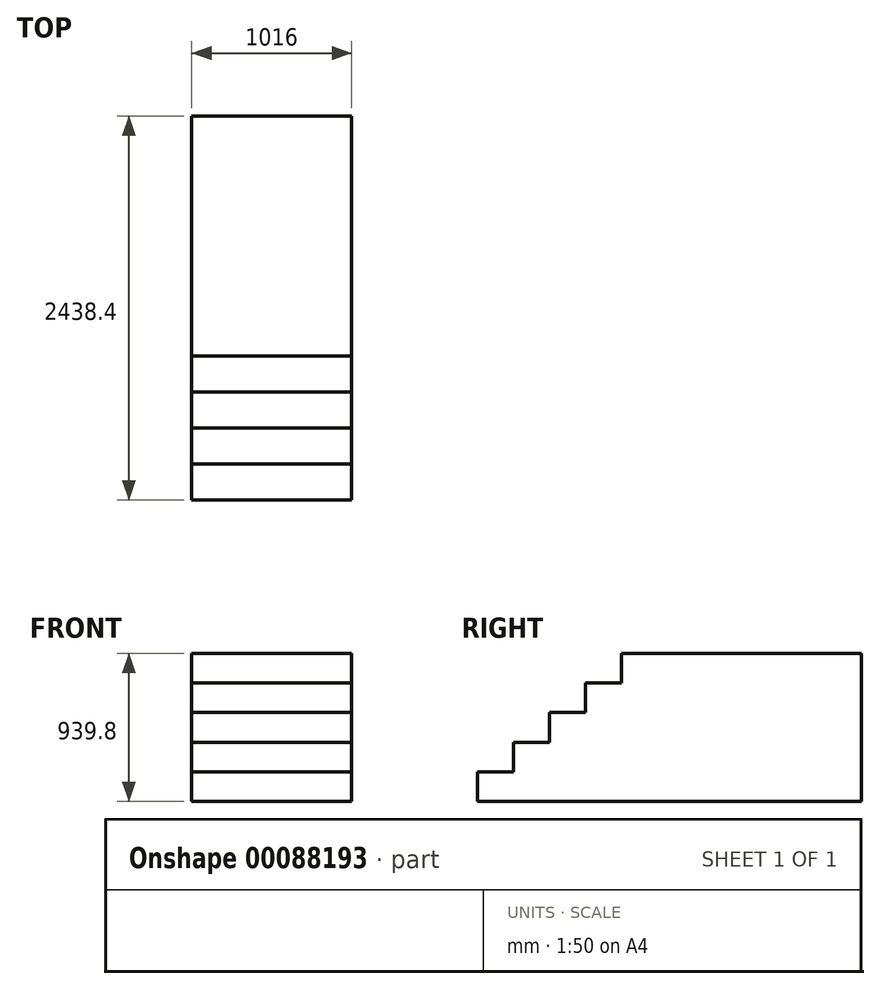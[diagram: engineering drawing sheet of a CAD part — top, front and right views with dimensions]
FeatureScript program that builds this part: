
annotation { "Feature Type Name" : "Feature", "Feature Type Description" : "" }
export const myFeature = defineFeature(function(context is Context, id is Id, definition is map)
    precondition{}
    {
        {
            var Q0;
            Q0=qCreatedBy(makeId("Top.planeOp"),FACE);
            var sketch = newSketch(context, id + "F0", { "sketchPlane" : qUnion([Q0])});
            skLineSegment(sketch, "E0.bottom", {"start": v(2438.4, -533.4) * mm, "end": v(-2438.4, -533.4) * mm});
            skLineSegment(sketch, "E0.top", {"start": v(2438.4, 533.4) * mm, "end": v(-2438.4, 533.4) * mm});
            skLineSegment(sketch, "E0.left", {"start": v(2438.4, -533.4) * mm, "end": v(2438.4, 533.4) * mm});
            skLineSegment(sketch, "E0.right", {"start": v(-2438.4, -533.4) * mm, "end": v(-2438.4, 533.4) * mm});
            skPoint(sketch, "E0.middle", {"position": v(0, 0) * mm});
            skSolve(sketch);
        }
        {
            var Q0;
            Q0=qSketchRegion(id+"F0",true);
            extrude(context, id + "F1", {"entities" : qUnion([Q0]), "oppositeDirection" : true, "depth" : 101.6 * mm});
        }
        {
            var Q0;
            Q0=makeQuery(id+"F1.opExtrude","SWEPT_FACE",FACE,{"disambiguationData":[OSD([sQuery(id+"F0.wireOp",EDGE,"E0.right")])]});
            var sketch = newSketch(context, id + "F2", { "sketchPlane" : qUnion([Q0])});
            skLineSegment(sketch, "E1", {"start": v(533.4, 0) * mm, "end": v(533.4, -187.96) * mm});
            skLineSegment(sketch, "E2", {"start": v(533.4, -187.96) * mm, "end": v(762, -187.96) * mm});
            skLineSegment(sketch, "E3", {"start": v(762, -187.96) * mm, "end": v(762, -375.92) * mm});
            skLineSegment(sketch, "E4", {"start": v(762, -375.92) * mm, "end": v(990.6, -375.92) * mm});
            skLineSegment(sketch, "E5", {"start": v(990.6, -375.92) * mm, "end": v(990.6, -563.88) * mm});
            skLineSegment(sketch, "E6", {"start": v(990.6, -563.88) * mm, "end": v(1219.2, -563.88) * mm});
            skLineSegment(sketch, "E7", {"start": v(1447.8, -751.84) * mm, "end": v(1447.8, -939.8) * mm});
            skLineSegment(sketch, "E8", {"start": v(1447.8, -939.8) * mm, "end": v(304.8, -939.8) * mm});
            skLineSegment(sketch, "E9", {"start": v(304.8, -939.8) * mm, "end": v(304.8, 0) * mm, "construction": true});
            skLineSegment(sketch, "E10", {"start": v(304.8, 0) * mm, "end": v(533.4, 0) * mm});
            skLineSegment(sketch, "E11", {"start": v(1219.2, -563.88) * mm, "end": v(1219.2, -751.84) * mm});
            skLineSegment(sketch, "E12", {"start": v(1219.2, -751.84) * mm, "end": v(1447.8, -751.84) * mm});
            skLineSegment(sketch, "E13", {"start": v(304.8, -939.8) * mm, "end": v(-533.4, -939.8) * mm});
            skLineSegment(sketch, "E14", {"start": v(-533.4, -939.8) * mm, "end": v(-533.4, 0) * mm});
            skLineSegment(sketch, "E15", {"start": v(-533.4, 0) * mm, "end": v(304.8, 0) * mm});
            skSolve(sketch);
        }
        {
            var Q0;
            Q0=qSketchRegion(id+"F2",true);
            extrude(context, id + "F3", {"entities" : qUnion([Q0]), "operationType" : NewBodyOperationType.ADD, "oppositeDirection" : true, "depth" : 1016 * mm});
        }
        {
            var Q0;
            Q0=makeQuery(id+"F3.boolean.opBoolean","MERGE",FACE,{"derivedFrom":[makeQuery(id+"F1.opExtrude","SWEPT_FACE",FACE,{"disambiguationData":[OSD([sQuery(id+"F0.wireOp",EDGE,"E0.bottom")])]}),makeQuery(id+"F3.opExtrude","SWEPT_FACE",FACE,{"disambiguationData":[OSD([sQuery(id+"F2.wireOp",EDGE,"E1")])]})]});
            var sketch = newSketch(context, id + "F4", { "sketchPlane" : qUnion([Q0])});
            skLineSegment(sketch, "E16.0", {"start": v(-1422.4, -101.6) * mm, "end": v(-1422.4, -187.96) * mm});
            skLineSegment(sketch, "E17", {"start": v(-1422.4, -101.6) * mm, "end": v(762, -101.6) * mm});
            skLineSegment(sketch, "E18", {"start": v(762, -101.6) * mm, "end": v(762, -939.8) * mm});
            skLineSegment(sketch, "E19", {"start": v(762, -939.8) * mm, "end": v(-1422.4, -939.8) * mm});
            skLineSegment(sketch, "E20", {"start": v(-1422.4, -187.96) * mm, "end": v(-1422.4, -939.8) * mm});
            skLineSegment(sketch, "E21.bottom", {"start": v(-812.8, -939.8) * mm, "end": v(-355.6, -939.8) * mm});
            skLineSegment(sketch, "E21.top", {"start": v(-812.8, -228.6) * mm, "end": v(-355.6, -228.6) * mm});
            skLineSegment(sketch, "E21.left", {"start": v(-812.8, -939.8) * mm, "end": v(-812.8, -228.6) * mm});
            skLineSegment(sketch, "E21.right", {"start": v(-355.6, -939.8) * mm, "end": v(-355.6, -228.6) * mm});
            skLineSegment(sketch, "E22.bottom", {"start": v(-304.8, -939.8) * mm, "end": v(152.4, -939.8) * mm});
            skLineSegment(sketch, "E22.top", {"start": v(-304.8, -228.6) * mm, "end": v(152.4, -228.6) * mm});
            skLineSegment(sketch, "E22.left", {"start": v(-304.8, -939.8) * mm, "end": v(-304.8, -228.6) * mm});
            skLineSegment(sketch, "E22.right", {"start": v(152.4, -939.8) * mm, "end": v(152.4, -228.6) * mm});
            skSolve(sketch);
        }
        {
            var Q0;
            Q0=makeQuery(id+"F4.imprint","IMPRINT",FACE,{"disambiguationData":[TD([[makeQuery(id+"F4.imprint","IMPRINT",EDGE,{"derivedFrom":sQuery(id+"F4.wireOp",EDGE,"E16.0")}),1.0]])]});
            extrude(context, id + "F5", {"entities" : qUnion([Q0]), "operationType" : NewBodyOperationType.ADD, "oppositeDirection" : true, "depth" : 101.6 * mm});
        }
        {
            var Q0;
            Q0=makeQuery(id+"F1.opExtrude","CAP_FACE",FACE,{"disambiguationData":[OSD([sQuery(id+"F0.wireOp",EDGE,"E0.bottom"),sQuery(id+"F0.wireOp",EDGE,"E0.top"),sQuery(id+"F0.wireOp",EDGE,"E0.left"),sQuery(id+"F0.wireOp",EDGE,"E0.right")])],"isStart":true});
            var sketch = newSketch(context, id + "F6", { "sketchPlane" : qUnion([Q0])});
            skLineSegment(sketch, "E23", {"start": v(-1422.4, -533.4) * mm, "end": v(-2438.4, 533.4) * mm});
            skLineSegment(sketch, "E24", {"start": v(-2438.4, 533.4) * mm, "end": v(-2438.4, -533.4) * mm});
            skLineSegment(sketch, "E25", {"start": v(-2438.4, -533.4) * mm, "end": v(-1422.4, -533.4) * mm});
            skSolve(sketch);
        }
        {
            var Q0;
            Q0=makeQuery(id+"F1.opExtrude","CAP_FACE",FACE,{"disambiguationData":[OSD([sQuery(id+"F0.wireOp",EDGE,"E0.bottom"),sQuery(id+"F0.wireOp",EDGE,"E0.top"),sQuery(id+"F0.wireOp",EDGE,"E0.left"),sQuery(id+"F0.wireOp",EDGE,"E0.right")])],"isStart":true});
            var sketch = newSketch(context, id + "F7", { "sketchPlane" : qUnion([Q0])});
            skLineSegment(sketch, "E26.0", {"start": v(2438.4, -533.4) * mm, "end": v(-1422.4, -533.4) * mm});
            skLineSegment(sketch, "E27.0", {"start": v(2438.4, -533.4) * mm, "end": v(2438.4, 533.4) * mm});
            skLineSegment(sketch, "E28.0", {"start": v(2438.4, 533.4) * mm, "end": v(-1422.4, 533.4) * mm});
            skLineSegment(sketch, "E29", {"start": v(-1422.4, -533.4) * mm, "end": v(-1422.4, 533.4) * mm});
            skPoint(sketch, "E30.orphan", {"position": v(-2438.4, 533.4) * mm});
            skPoint(sketch, "E31.orphan", {"position": v(-2438.4, -533.4) * mm});
            skSolve(sketch);
        }
        {
            var Q0;
            Q0 = qSketchRegion(id + "F7", true);
            extrude(context, id + "F8", {"entities" : qUnion([Q0]), "operationType" : NewBodyOperationType.REMOVE, "oppositeDirection" : true, "depth" : 458.42 * mm});
        }
        {
            var Q0;
            Q0=makeQuery(id+"F3.boolean.opBoolean","MERGE",FACE,{"derivedFrom":[makeQuery(id+"F1.opExtrude","SWEPT_FACE",FACE,{"disambiguationData":[OSD([sQuery(id+"F0.wireOp",EDGE,"E0.top")])]}),makeQuery(id+"F3.opExtrude","SWEPT_FACE",FACE,{"disambiguationData":[OSD([sQuery(id+"F2.wireOp",EDGE,"E14")])]})]});
            var sketch = newSketch(context, id + "F9", { "sketchPlane" : qUnion([Q0])});
            skLineSegment(sketch, "E32.0", {"start": v(1422.4, -939.8) * mm, "end": v(1422.4, 0) * mm});
            skLineSegment(sketch, "E33.0", {"start": v(1422.4, 0) * mm, "end": v(2438.4, 0) * mm});
            skLineSegment(sketch, "E34.0", {"start": v(2438.4, -939.8) * mm, "end": v(2438.4, 0) * mm});
            skLineSegment(sketch, "E35.0", {"start": v(1422.4, -939.8) * mm, "end": v(2438.4, -939.8) * mm});
            skSolve(sketch);
        }
        {
            var Q0;
            Q0 = qSketchRegion(id + "F9", true);
            extrude(context, id + "F10", {"entities" : qUnion([Q0]), "operationType" : NewBodyOperationType.ADD, "depth" : 457.2 * mm});
        }
    });
